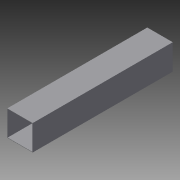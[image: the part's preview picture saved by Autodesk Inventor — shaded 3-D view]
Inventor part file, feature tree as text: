
AUTODESK INVENTOR PART (.ipt)
format: ipt  version: 2016 (Build 200138000, 138)  size: 107,008 bytes
history: native  units: in
note: dims shown in document units (in); Inventor stores cm internally (conversion verified against a paired STEP export)
features: sketch x4, extrude x3
ambient origin geometry x8: Origin, YZ Plane, XZ Plane, XY Plane, X Axis, Y Axis, Z Axis, Center Point
bodies: Solid1 (feature_tree)
feature tree (7):
  extrude  "Extrusion1"  Depth=2.0in
  extrude  "Extrusion2"  Depth=11.0in TaperAngle=0.0deg
  sketch  "Sketch3"  dims[d5=2.0in d6=0.03in]
  extrude  "Extrusion3"  Depth=0.03in
  sketch  "Sketch1"  dims[d0=2.0in d1=2.0in]
  sketch  "Sketch2"  dims[d2=0.03in d3=11.0in d4=0.0in]
  sketch  "Sketch4"  dims[d7=3.5in d8=0.0in d9=2.0in d10=0.03in d11=7.0in d12=0.0in]
